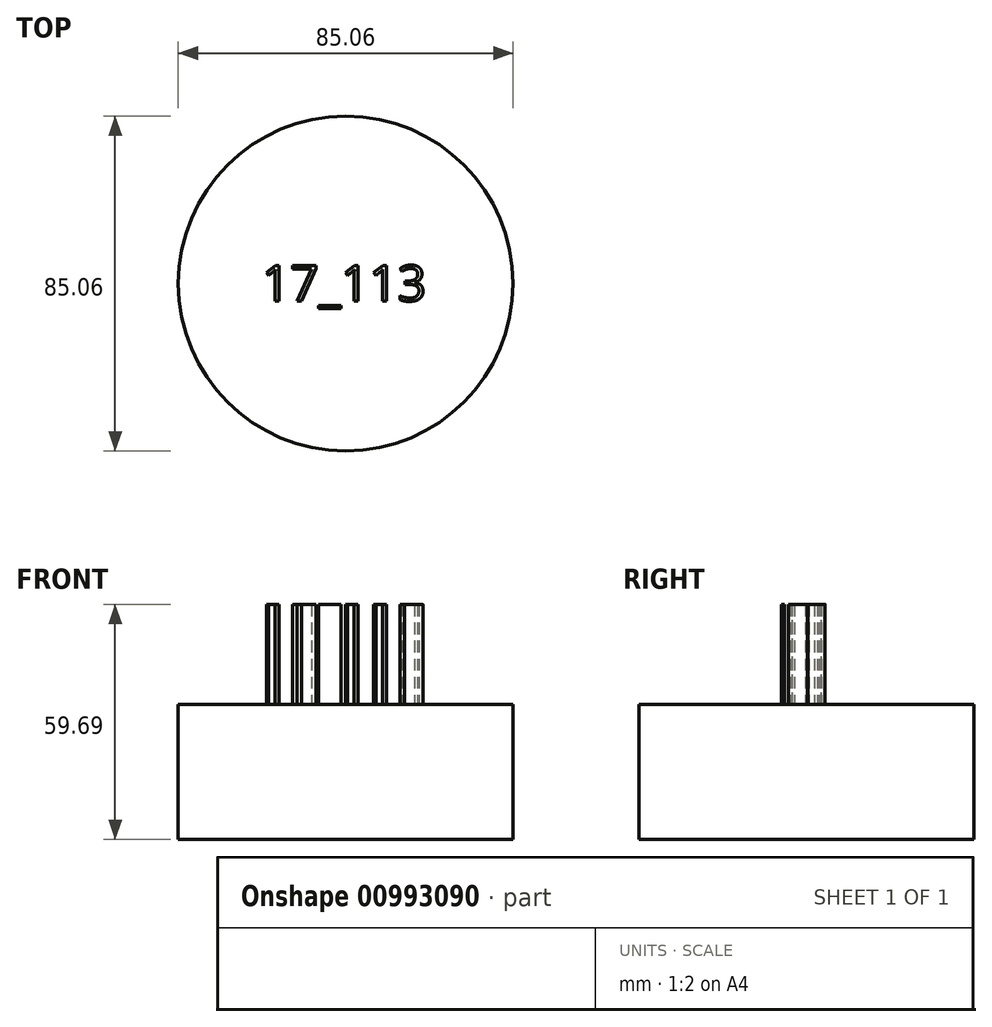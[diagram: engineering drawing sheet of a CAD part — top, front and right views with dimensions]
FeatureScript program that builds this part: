
annotation { "Feature Type Name" : "Feature", "Feature Type Description" : "" }
export const myFeature = defineFeature(function(context is Context, id is Id, definition is map)
    precondition{}
    {
        {
            var Q0;
            Q0=qCreatedBy(makeId("Top.planeOp"),FACE);
            var sketch = newSketch(context, id + "F0", { "sketchPlane" : qUnion([Q0])});
            skCircle(sketch, "E0", {"center": v(0, 0) * mm, "radius": 42.53 * mm});
            skSolve(sketch);
        }
        {
            var Q0;
            Q0=makeQuery(id+"F0.imprint","IMPRINT",FACE,{"disambiguationData":[TD([[makeQuery(id+"F0.imprint","IMPRINT",EDGE,{"derivedFrom":sQuery(id+"F0.wireOp",EDGE,"E0")}),1.0]])]});
            extrude(context, id + "F1", {"entities" : qUnion([Q0]), "depth" : 34.3 * mm, "offsetDistance" : 25.4 * mm});
        }
        {
            var Q0;
            Q0=makeQuery(id+"F1.opExtrude","CAP_FACE",FACE,{"disambiguationData":[OSD([sQuery(id+"F0.wireOp",EDGE,"E0")])],"isStart":false});
            var sketch = newSketch(context, id + "F2", { "sketchPlane" : qUnion([Q0])});
            skText(sketch, "E1", { "text": "17_113", "fontName": "OpenSans-Regular.ttf"});
            const initialGuessF2  = {"E1": [-0.02133, -0.00443, 1, 0, 0.00908]};
            skSetInitialGuess(sketch, initialGuessF2);
            skSolve(sketch);
        }
        {
            var Q0;
            Q0 = qSketchRegion(id + "F2", true);
            extrude(context, id + "F3", {"entities" : qUnion([Q0]), "depth" : 25.4 * mm, "offsetDistance" : 25.4 * mm});
        }
    });
